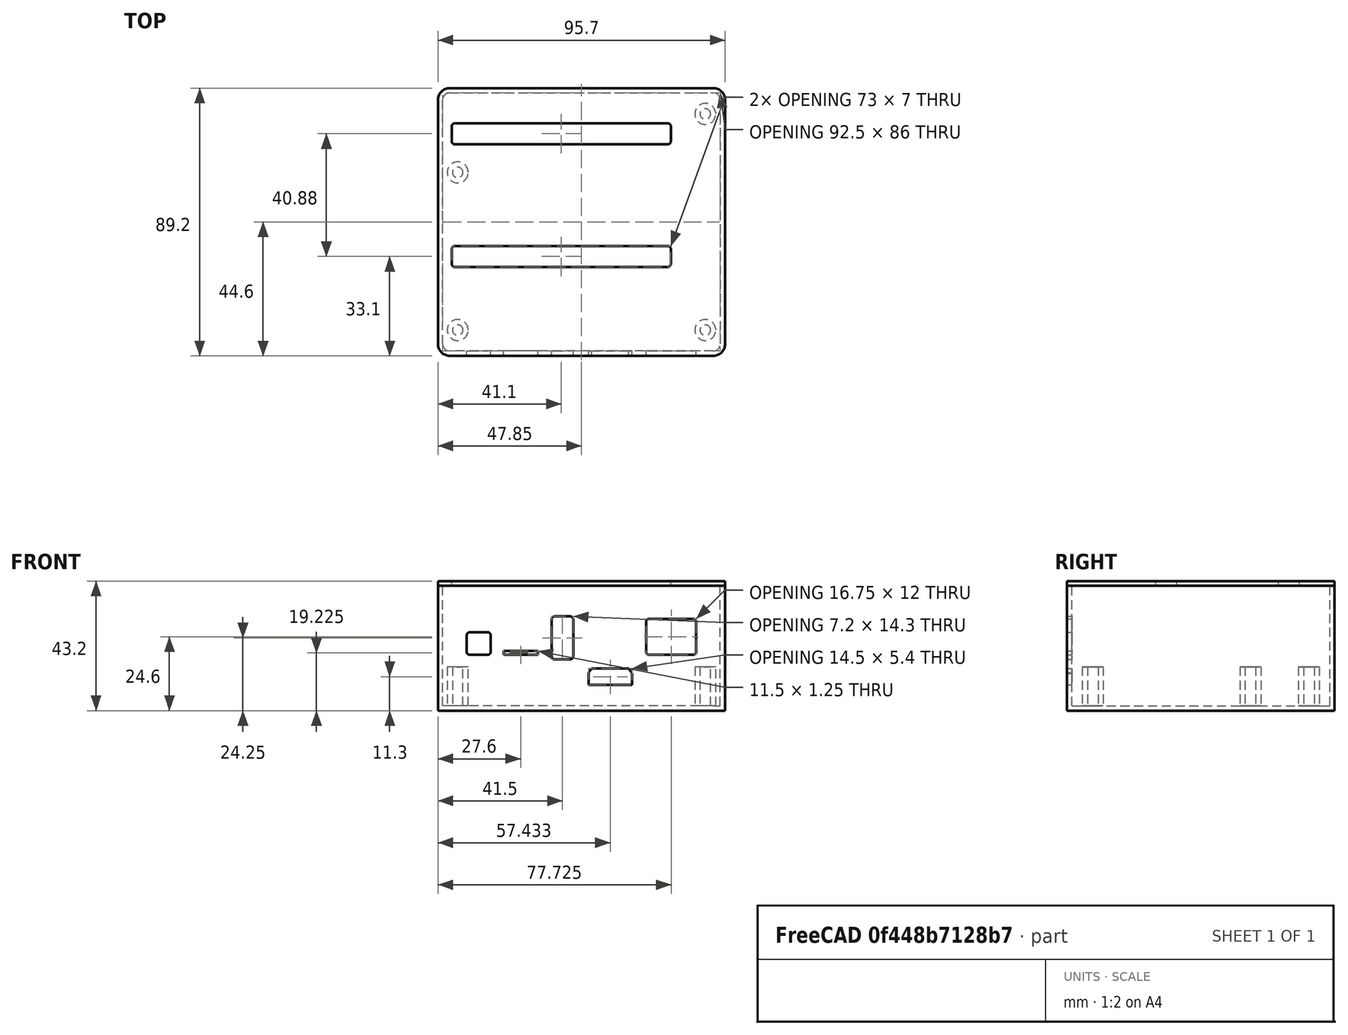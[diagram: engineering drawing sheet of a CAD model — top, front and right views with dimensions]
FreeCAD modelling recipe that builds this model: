
FCSTD DOCUMENT  (FreeCAD 0.16R6712 (Git))
Label: odroid-hc4-enclosure-with-lid
License: All rights reserved
LicenseURL: http://en.wikipedia.org/wiki/All_rights_reserved
objects: Sketcher::SketchObject×6, PartDesign::Pad×5, Part::Thickness×1, Part::Cut×1, PartDesign::Fillet×1, Mesh::Feature×1, Part::Part2DObjectPython×1
note: 20 computed .brp shape members not serialized (recipe doc carries the construction recipe); baked Part::Feature solids carry a one-line shape summary decoded from their .brp

FEATURE [Sketcher::SketchObject] Sketch  label="Sketch - Board"
  expr: Constraints[50] = Sketch.Constraints.SataX
  expr: Constraints[51] = Sketch.Constraints.SataY
  expr: Constraints[52] = Sketch.Constraints.SataOffsetX
  sketch-geometry (20):
    g0: LineSegment StartX=-39.25 StartY=42 StartZ=0 EndX=39.25 EndY=42 EndZ=0
    g1: LineSegment StartX=45.25 StartY=36 StartZ=0 EndX=45.25 EndY=-36 EndZ=0
    g2: LineSegment StartX=39.25 StartY=-42 StartZ=0 EndX=-39.25 EndY=-42 EndZ=0
    g3: LineSegment StartX=-45.25 StartY=-36 StartZ=0 EndX=-45.25 EndY=36 EndZ=0
    g4: ArcOfCircle CenterX=-39.25 CenterY=-36 CenterZ=0 NormalX=0 NormalY=0 NormalZ=1 Radius=6 StartAngle=3.14159 EndAngle=4.71239
    g5: ArcOfCircle CenterX=39.25 CenterY=-36 CenterZ=0 NormalX=0 NormalY=0 NormalZ=1 Radius=6 StartAngle=4.71239 EndAngle=6.28319
    g6: ArcOfCircle CenterX=39.25 CenterY=36 CenterZ=0 NormalX=0 NormalY=0 NormalZ=1 Radius=6 StartAngle=0 EndAngle=1.5708
    g7: ArcOfCircle CenterX=-39.25 CenterY=36 CenterZ=0 NormalX=0 NormalY=0 NormalZ=1 Radius=6 StartAngle=1.5708 EndAngle=3.14159
    g8: Circle CenterX=-41.25 CenterY=-36 CenterZ=0 NormalX=0 NormalY=0 NormalZ=1 Radius=1.75
    g9: Circle CenterX=41.25 CenterY=-36 CenterZ=0 NormalX=0 NormalY=0 NormalZ=1 Radius=1.75
    g10: Circle CenterX=-41.25 CenterY=16.5 CenterZ=0 NormalX=0 NormalY=0 NormalZ=1 Radius=1.75
    g11: Circle CenterX=41.25 CenterY=36 CenterZ=0 NormalX=0 NormalY=0 NormalZ=1 Radius=1.75
    g12: LineSegment StartX=-24.4 StartY=-9 StartZ=0 EndX=19.25 EndY=-9 EndZ=0
    g13: LineSegment StartX=19.25 StartY=-9 StartZ=0 EndX=19.25 EndY=-14 EndZ=0
    g14: LineSegment StartX=19.25 StartY=-14 StartZ=0 EndX=-24.4 EndY=-14 EndZ=0
    g15: LineSegment StartX=-24.4 StartY=-14 StartZ=0 EndX=-24.4 EndY=-9 EndZ=0
    g16: LineSegment StartX=-24.4 StartY=31.88 StartZ=0 EndX=19.25 EndY=31.88 EndZ=0
    g17: LineSegment StartX=19.25 StartY=31.88 StartZ=0 EndX=19.25 EndY=26.88 EndZ=0
    g18: LineSegment StartX=19.25 StartY=26.88 StartZ=0 EndX=-24.4 EndY=26.88 EndZ=0
    g19: LineSegment StartX=-24.4 StartY=26.88 StartZ=0 EndX=-24.4 EndY=31.88 EndZ=0
  constraints (54):
    c: Horizontal(g0)
    c: Horizontal(g2)
    c: Vertical(g1)
    c: Vertical(g3)
    c: Tangent(g3,g4) = 1.5708
    c: Tangent(g2,g4) = 1.5708
    c: Tangent(g2,g5) = 1.5708
    c: Tangent(g1,g5) = 1.5708
    c: Tangent(g0,g6) = 1.5708
    c: Tangent(g1,g6) = 1.5708
    c: Tangent(g3,g7) = 1.5708
    c: Tangent(g0,g7) = 1.5708
    c: Symmetric(g3,g1,g-2)
    c: Symmetric(g2,g0,g-1)
    c: Radius(g6) = 6
    c: Equal(g6,g7)
    c: DistanceX(g3,g1) = 90.5  'X'
    c: DistanceY(g2,g0) = 84  'Y'
    c: Radius(g9) = 1.75  'Constraint20'
    c: Equal(g9,g8)
    c: Equal(g9,g10)
    c: Equal(g9,g11)
    c: DistanceY(g2,g9) = 6  'Y1'
    c: DistanceX(g9,g1) = 4  'X1'
    c: DistanceY(g2,g8) = 6  'Y4'
    c: DistanceX(g3,g8) = 4  'X4'
    c: DistanceX(g11,g1) = 4  'X2'
    c: DistanceY(g11,g0) = 6  'Y2'
    c: DistanceX(g3,g10) = 4  'X3'
    c: DistanceY(g10,g0) = 25.5  'Y3'
    c: Coincident(g12,g13)
    c: Coincident(g13,g14)
    c: Coincident(g14,g15)
    c: Coincident(g15,g12)
    c: Horizontal(g12)
    c: Horizontal(g14)
    c: Vertical(g13)
    c: Vertical(g15)
    c: DistanceX(g14,g13) = 43.65  'SataX'
    c: DistanceX(g13,g1) = 26  'SataOffsetX'
    c: DistanceY(g14,g12) = 5  'SataY'
    c: DistanceY(g2,g13) = 28  'SataoffsetY'
    c: Coincident(g16,g17)
    c: Coincident(g17,g18)
    c: Coincident(g18,g19)
    c: Coincident(g19,g16)
    c: Horizontal(g16)
    c: Horizontal(g18)
    c: Vertical(g17)
    c: Vertical(g19)
    c: DistanceX(g18,g17) = 43.65
    c: DistanceY(g18,g16) = 5
    c: DistanceX(g17,g1) = 26
    c: DistanceY(g16,g0) = 10.12  'Sata2OffsetY'
FEATURE [Sketcher::SketchObject] Sketch001  label="Sketch - Walls"
  expr: Constraints.X = Sketch.Constraints.X + 2 + 3.2
  expr: Constraints.Y = Sketch.Constraints.Y + 2 + 3.2
  sketch-geometry (8):
    g0: LineSegment StartX=-43.85 StartY=44.6 StartZ=0 EndX=43.85 EndY=44.6 EndZ=0
    g1: LineSegment StartX=47.85 StartY=40.6 StartZ=0 EndX=47.85 EndY=-40.6 EndZ=0
    g2: LineSegment StartX=43.85 StartY=-44.6 StartZ=0 EndX=-43.85 EndY=-44.6 EndZ=0
    g3: LineSegment StartX=-47.85 StartY=-40.6 StartZ=0 EndX=-47.85 EndY=40.6 EndZ=0
    g4: ArcOfCircle CenterX=-43.85 CenterY=-40.6 CenterZ=0 NormalX=0 NormalY=0 NormalZ=1 Radius=4 StartAngle=3.14159 EndAngle=4.71239
    g5: ArcOfCircle CenterX=43.85 CenterY=-40.6 CenterZ=0 NormalX=0 NormalY=0 NormalZ=1 Radius=4 StartAngle=4.71239 EndAngle=6.28319
    g6: ArcOfCircle CenterX=43.85 CenterY=40.6 CenterZ=0 NormalX=0 NormalY=0 NormalZ=1 Radius=4 StartAngle=0 EndAngle=1.5708
    g7: ArcOfCircle CenterX=-43.85 CenterY=40.6 CenterZ=0 NormalX=0 NormalY=0 NormalZ=1 Radius=4 StartAngle=1.5708 EndAngle=3.14159
  constraints (19):
    c: Horizontal(g0)
    c: Horizontal(g2)
    c: Vertical(g1)
    c: Vertical(g3)
    c: Tangent(g3,g4) = 1.5708
    c: Tangent(g2,g4) = 1.5708
    c: Tangent(g2,g5) = 1.5708
    c: Tangent(g1,g5) = 1.5708
    c: Tangent(g1,g6) = 1.5708
    c: Tangent(g0,g6) = 1.5708
    c: Tangent(g3,g7) = 1.5708
    c: Tangent(g0,g7) = 1.5708
    c: Radius(g7) = 4
    c: Equal(g7,g6)
    c: Equal(g7,g5)
    c: DistanceX(g3,g1) = 95.7  'X'
    c: DistanceY(g2,g0) = 89.2  'Y'
    c: Symmetric(g2,g0,g-1)  'Constraint18'
    c: Symmetric(g3,g1,g-2)
FEATURE [PartDesign::Pad] Pad
  Length = 40
  Length2 = 1.6
  Sketch = -> Sketch001
  Type = 4
FEATURE [Part::Thickness] Thickness
  Faces = -> Pad [Face10]
  Intersection = false
  Join = 0
  Mode = 0
  SelfIntersection = false
  Value = -1.6
FEATURE [Sketcher::SketchObject] Sketch002  label="Sketch - Legs"
  Support = -> Thickness [Face19]
  expr: Constraints[24] = Sketch.Constraints.Y4
  expr: Constraints[29] = Sketch.Constraints.Y3
  expr: Constraints[28] = Sketch.Constraints.X3
  expr: Constraints[26] = Sketch.Constraints.X2
  expr: Constraints[27] = Sketch.Constraints.Y2
  expr: Constraints[25] = Sketch.Constraints.X4
  expr: Constraints[22] = Sketch.Constraints.Y1
  expr: Constraints.Y = Sketch.Constraints.Y
  expr: Constraints[23] = Sketch.Constraints.X1
  expr: Constraints.X = Sketch.Constraints.X
  sketch-geometry (12):
    g0: LineSegment [constr] StartX=-39.25 StartY=42 StartZ=0 EndX=39.25 EndY=42 EndZ=0
    g1: LineSegment [constr] StartX=45.25 StartY=36 StartZ=0 EndX=45.25 EndY=-36 EndZ=0
    g2: LineSegment [constr] StartX=39.25 StartY=-42 StartZ=0 EndX=-39.25 EndY=-42 EndZ=0
    g3: LineSegment [constr] StartX=-45.25 StartY=-36 StartZ=0 EndX=-45.25 EndY=36 EndZ=0
    g4: ArcOfCircle [constr] CenterX=-39.25 CenterY=-36 CenterZ=0 NormalX=0 NormalY=0 NormalZ=1 Radius=6 StartAngle=3.14159 EndAngle=4.71239
    g5: ArcOfCircle [constr] CenterX=39.25 CenterY=-36 CenterZ=0 NormalX=0 NormalY=0 NormalZ=1 Radius=6 StartAngle=4.71239 EndAngle=6.28319
    g6: ArcOfCircle [constr] CenterX=39.25 CenterY=36 CenterZ=0 NormalX=0 NormalY=0 NormalZ=1 Radius=6 StartAngle=0 EndAngle=1.5708
    g7: ArcOfCircle [constr] CenterX=-39.25 CenterY=36 CenterZ=0 NormalX=0 NormalY=0 NormalZ=1 Radius=6 StartAngle=1.5708 EndAngle=3.14159
    g8: Circle CenterX=-41.25 CenterY=-36 CenterZ=0 NormalX=0 NormalY=0 NormalZ=1 Radius=1.75
    g9: Circle CenterX=41.25 CenterY=-36 CenterZ=0 NormalX=0 NormalY=0 NormalZ=1 Radius=1.75
    g10: Circle CenterX=-41.25 CenterY=16.5 CenterZ=0 NormalX=0 NormalY=0 NormalZ=1 Radius=1.75
    g11: Circle CenterX=41.25 CenterY=36 CenterZ=0 NormalX=0 NormalY=0 NormalZ=1 Radius=1.75
  constraints (30):
    c: Horizontal(g0)
    c: Horizontal(g2)
    c: Vertical(g1)
    c: Vertical(g3)
    c: Tangent(g3,g4) = 1.5708
    c: Tangent(g2,g4) = 1.5708
    c: Tangent(g2,g5) = 1.5708
    c: Tangent(g1,g5) = 1.5708
    c: Tangent(g0,g6) = 1.5708
    c: Tangent(g1,g6) = 1.5708
    c: Tangent(g3,g7) = 1.5708
    c: Tangent(g0,g7) = 1.5708
    c: Symmetric(g3,g1,g-2)
    c: Symmetric(g2,g0,g-1)
    c: Radius(g6) = 6
    c: Equal(g6,g7)
    c: DistanceX(g3,g1) = 90.5  'X'
    c: DistanceY(g2,g0) = 84  'Y'
    c: Radius(g9) = 1.75  'Constraint20'
    c: Equal(g9,g8)
    c: Equal(g9,g10)
    c: Equal(g9,g11)
    c: DistanceY(g2,g9) = 6
    c: DistanceX(g9,g1) = 4
    c: DistanceY(g2,g8) = 6
    c: DistanceX(g3,g8) = 4
    c: DistanceX(g11,g1) = 4
    c: DistanceY(g11,g0) = 6
    c: DistanceX(g3,g10) = 4
    c: DistanceY(g10,g0) = 25.5
FEATURE [PartDesign::Pad] Pad001
  Length = 13
  Length2 = 100
  Sketch = -> Sketch002
  Type = 0
FEATURE [Sketcher::SketchObject] Sketch003  label="Sketch - Wide Legs"
  ExternalGeometry = -> [Pad001]
  Support = -> Pad001 [Face19]
  sketch-geometry (4):
    g0: Circle CenterX=41.25 CenterY=-36 CenterZ=0 NormalX=0 NormalY=0 NormalZ=1 Radius=3.5
    g1: Circle CenterX=41.25 CenterY=36 CenterZ=0 NormalX=0 NormalY=0 NormalZ=1 Radius=3.5
    g2: Circle CenterX=-41.25 CenterY=16.5 CenterZ=0 NormalX=0 NormalY=0 NormalZ=1 Radius=3.5
    g3: Circle CenterX=-41.25 CenterY=-36 CenterZ=0 NormalX=0 NormalY=0 NormalZ=1 Radius=3.5
  constraints (8):
    c: Coincident(g0,g-5)
    c: Coincident(g1,g-6)
    c: Coincident(g2,g-3)
    c: Coincident(g3,g-4)
    c: Radius(g2) = 3.5
    c: Equal(g2,g1)
    c: Equal(g2,g0)
    c: Equal(g2,g3)
FEATURE [PartDesign::Pad] Pad002
  Length = 13
  Length2 = 100
  Sketch = -> Sketch003
  Type = 0
FEATURE [Sketcher::SketchObject] Sketch004
  Placement = pos=(0,-44.6,0) rot=(1,0,0;1.5708rad)
  sketch-geometry (40):
    g0: LineSegment StartX=22.5 StartY=29 StartZ=0 EndX=37.25 EndY=29 EndZ=0
    g1: LineSegment StartX=38.25 StartY=28 StartZ=0 EndX=38.25 EndY=18 EndZ=0
    g2: LineSegment StartX=37.25 StartY=17 StartZ=0 EndX=22.5 EndY=17 EndZ=0
    g3: LineSegment StartX=21.5 StartY=18 StartZ=0 EndX=21.5 EndY=28 EndZ=0
    g4: LineSegment StartX=-8.95 StartY=29.8 StartZ=0 EndX=-3.75 EndY=29.8 EndZ=0
    g5: LineSegment StartX=-2.75 StartY=28.8 StartZ=0 EndX=-2.75 EndY=16.5 EndZ=0
    g6: LineSegment StartX=-3.75 StartY=15.5 StartZ=0 EndX=-8.95 EndY=15.5 EndZ=0
    g7: LineSegment StartX=-9.95 StartY=16.5 StartZ=0 EndX=-9.95 EndY=28.8 EndZ=0
    g8: LineSegment StartX=-37.25 StartY=24.5 StartZ=0 EndX=-31.25 EndY=24.5 EndZ=0
    g9: LineSegment StartX=-30.25 StartY=23.5 StartZ=0 EndX=-30.25 EndY=18 EndZ=0
    g10: LineSegment StartX=-31.25 StartY=17 StartZ=0 EndX=-37.25 EndY=17 EndZ=0
    g11: LineSegment StartX=-38.25 StartY=18 StartZ=0 EndX=-38.25 EndY=23.5 EndZ=0
    g12: LineSegment StartX=-26 StartY=18.25 StartZ=0 EndX=-14.5 EndY=18.25 EndZ=0
    g13: LineSegment StartX=-14.5 StartY=18.25 StartZ=0 EndX=-14.5 EndY=17 EndZ=0
    g14: LineSegment StartX=-14.5 StartY=17 StartZ=0 EndX=-26 EndY=17 EndZ=0
    g15: LineSegment StartX=-26 StartY=17 StartZ=0 EndX=-26 EndY=18.25 EndZ=0
    g16: ArcOfCircle CenterX=37.25 CenterY=18 CenterZ=0 NormalX=0 NormalY=0 NormalZ=1 Radius=1 StartAngle=4.71239 EndAngle=6.28319
    g17: ArcOfCircle CenterX=37.25 CenterY=28 CenterZ=0 NormalX=0 NormalY=0 NormalZ=1 Radius=1 StartAngle=0 EndAngle=1.5708
    g18: ArcOfCircle CenterX=22.5 CenterY=28 CenterZ=0 NormalX=0 NormalY=0 NormalZ=1 Radius=1 StartAngle=1.5708 EndAngle=3.14159
    g19: ArcOfCircle CenterX=22.5 CenterY=18 CenterZ=0 NormalX=0 NormalY=0 NormalZ=1 Radius=1 StartAngle=3.14159 EndAngle=4.71239
    g20: ArcOfCircle CenterX=-8.95 CenterY=16.5 CenterZ=0 NormalX=0 NormalY=0 NormalZ=1 Radius=1 StartAngle=3.14159 EndAngle=4.71239
    g21: ArcOfCircle CenterX=-3.75 CenterY=16.5 CenterZ=0 NormalX=0 NormalY=0 NormalZ=1 Radius=1 StartAngle=4.71239 EndAngle=6.28319
    g22: ArcOfCircle CenterX=-3.75 CenterY=28.8 CenterZ=0 NormalX=0 NormalY=0 NormalZ=1 Radius=1 StartAngle=0 EndAngle=1.5708
    g23: ArcOfCircle CenterX=-8.95 CenterY=28.8 CenterZ=0 NormalX=0 NormalY=0 NormalZ=1 Radius=1 StartAngle=1.5708 EndAngle=3.14159
    g24: ArcOfCircle CenterX=-37.25 CenterY=18 CenterZ=0 NormalX=0 NormalY=0 NormalZ=1 Radius=1 StartAngle=3.14159 EndAngle=4.71239
    g25: ArcOfCircle CenterX=-31.25 CenterY=18 CenterZ=0 NormalX=0 NormalY=0 NormalZ=1 Radius=1 StartAngle=4.71239 EndAngle=6.28319
    g26: ArcOfCircle CenterX=-31.25 CenterY=23.5 CenterZ=0 NormalX=0 NormalY=0 NormalZ=1 Radius=1 StartAngle=0 EndAngle=1.5708
    g27: ArcOfCircle CenterX=-37.25 CenterY=23.5 CenterZ=0 NormalX=0 NormalY=0 NormalZ=1 Radius=1 StartAngle=1.5708 EndAngle=3.14159
    g28: GeomPoint [constr] X=2.3334 Y=7 Z=0
    g29: GeomPoint [constr] X=16.8334 Y=7 Z=0
    g30: GeomPoint [constr] X=2.3334 Y=11.0069 Z=0
    g31: GeomPoint [constr] X=3.39176 Y=12.4 Z=0
    g32: GeomPoint [constr] X=15.7519 Y=12.4 Z=0
    g33: GeomPoint [constr] X=16.8334 Y=10.8557 Z=0
    g34: LineSegment StartX=2.3334 StartY=7 StartZ=0 EndX=2.3334 EndY=11.0069 EndZ=0
    g35: LineSegment StartX=2.3334 StartY=11.0069 StartZ=0 EndX=3.39176 EndY=12.4 EndZ=0
    g36: LineSegment StartX=3.39176 StartY=12.4 StartZ=0 EndX=15.7519 EndY=12.4 EndZ=0
    g37: LineSegment StartX=15.7519 StartY=12.4 StartZ=0 EndX=16.8334 EndY=10.8557 EndZ=0
    g38: LineSegment StartX=16.8334 StartY=10.8557 StartZ=0 EndX=16.8334 EndY=7 EndZ=0
    g39: LineSegment StartX=16.8334 StartY=7 StartZ=0 EndX=2.3334 EndY=7 EndZ=0
  constraints (91):
    c: Horizontal(g0)
    c: Horizontal(g2)
    c: Vertical(g1)
    c: Vertical(g3)
    c: Horizontal(g4)
    c: Horizontal(g6)
    c: Vertical(g5)
    c: Vertical(g7)
    c: Horizontal(g8)
    c: Horizontal(g10)
    c: Vertical(g9)
    c: Vertical(g11)
    c: Coincident(g12,g13)
    c: Coincident(g13,g14)
    c: Coincident(g14,g15)
    c: Coincident(g15,g12)
    c: Horizontal(g12)
    c: Horizontal(g14)
    c: Vertical(g13)
    c: Vertical(g15)
    c: DistanceX(g14,g-1) = 26
    c: DistanceX(g14,g14) = 11.5
    c: Tangent(g2,g16) = 1.5708
    c: Tangent(g1,g16) = 1.5708
    c: Tangent(g0,g17) = 1.5708
    c: Tangent(g1,g17) = 1.5708
    c: Tangent(g3,g18) = 1.5708
    c: Tangent(g0,g18) = 1.5708
    c: Tangent(g3,g19) = 1.5708
    c: Tangent(g2,g19) = 1.5708
    c: DistanceX(g-1,g1) = 38.25
    c: DistanceX(g3,g1) = 16.75
    c: DistanceY(g2,g0) = 12
    c: DistanceY(g-1,g2) = 17
    c: Radius(g17) = 1
    c: Equal(g17,g16)
    c: Equal(g17,g19)
    c: Equal(g17,g18)
    c: Tangent(g7,g20) = 1.5708
    c: Tangent(g6,g20) = 1.5708
    c: Tangent(g6,g21) = 1.5708
    c: Tangent(g5,g21) = 1.5708
    c: Tangent(g4,g22) = 1.5708
    c: Tangent(g5,g22) = 1.5708
    c: Tangent(g7,g23) = 1.5708
    c: Tangent(g4,g23) = 1.5708
    c: DistanceX(g5,g-1) = 2.75
    c: DistanceY(g-1,g6) = 15.5
    c: DistanceX(g7,g5) = 7.2
    c: DistanceY(g6,g4) = 14.3
    c: Radius(g21) = 1
    c: Equal(g21,g22)
    c: Equal(g21,g23)
    c: Equal(g21,g20)
    c: Tangent(g11,g24) = 1.5708
    c: Tangent(g10,g24) = 1.5708
    c: Tangent(g10,g25) = 1.5708
    c: Tangent(g9,g25) = 1.5708
    c: Tangent(g9,g26) = 1.5708
    c: Tangent(g8,g26) = 1.5708
    c: Tangent(g11,g27) = 1.5708
    c: Tangent(g8,g27) = 1.5708
    c: DistanceX(g9,g-1) = 30.25
    c: DistanceY(g10,g8) = 7.5
    c: DistanceX(g11,g9) = 8
    c: DistanceY(g-1,g10) = 17
    c: Radius(g25) = 1
    c: Equal(g25,g24)
    c: Equal(g25,g27)
    c: Equal(g25,g26)
    c: DistanceY(g-1,g14) = 17
    c: DistanceY(g14,g12) = 1.25
    c: Coincident(g34,g28)
    c: Coincident(g34,g30)
    c: Vertical(g34)
    c: Coincident(g34,g35)
    c: Coincident(g35,g31)
    c: Coincident(g35,g36)
    c: Coincident(g36,g32)
    c: Horizontal(g36)
    c: Coincident(g36,g37)
    c: Coincident(g37,g33)
    c: Coincident(g37,g38)
    c: Coincident(g38,g29)
    c: Vertical(g38)
    c: Coincident(g38,g39)
    c: Coincident(g39,g34)
    c: Horizontal(g39)
    c: DistanceX(g28,g29) = 14.5
    c: DistanceY(g-1,g28) = 7
    c: DistanceY(g28,g31) = 5.4
FEATURE [PartDesign::Pad] Pad003
  Length = 3
  Length2 = 100
  Placement = pos=(0,-44.6,0) rot=(1,0,0;1.5708rad)
  Reversed = true
  Sketch = -> Sketch004
  Type = 0
FEATURE [Part::Cut] Cut
  Base = -> Pad002
  Tool = -> Pad003
FEATURE [PartDesign::Fillet] Fillet
  Base = -> Cut [Edge3,Edge9,Edge11,Edge12,Edge13,Edge14,Edge15,Edge6]
  Radius = 0.6
FEATURE [Mesh::Feature] Odroid_HC4  label="Odroid-HC4"
  Placement = pos=(-45.25,-42,11) rot=(0,0,1;0rad)
FEATURE [Sketcher::SketchObject] Sketch005  label="Sketch - Top Lid"
  Placement = pos=(0,0,40) rot=(0,0,1;0rad)
  Support = -> Pad [Face10]
  expr: Constraints[58] = Sketch.Constraints.Sata2OffsetY + 1 + 1.6 - 1
  expr: Constraints.Y = Sketch.Constraints.Y + 2 + 3.2
  expr: Constraints.X = Sketch.Constraints.X + 2 + 3.2
  sketch-geometry (24):
    g0: LineSegment StartX=-43.85 StartY=44.6 StartZ=0 EndX=43.85 EndY=44.6 EndZ=0
    g1: LineSegment StartX=47.85 StartY=40.6 StartZ=0 EndX=47.85 EndY=-40.6 EndZ=0
    g2: LineSegment StartX=43.85 StartY=-44.6 StartZ=0 EndX=-43.85 EndY=-44.6 EndZ=0
    g3: LineSegment StartX=-47.85 StartY=-40.6 StartZ=0 EndX=-47.85 EndY=40.6 EndZ=0
    g4: ArcOfCircle CenterX=-43.85 CenterY=-40.6 CenterZ=0 NormalX=0 NormalY=0 NormalZ=1 Radius=4 StartAngle=3.14159 EndAngle=4.71239
    g5: ArcOfCircle CenterX=43.85 CenterY=-40.6 CenterZ=0 NormalX=0 NormalY=0 NormalZ=1 Radius=4 StartAngle=4.71239 EndAngle=6.28319
    g6: ArcOfCircle CenterX=43.85 CenterY=40.6 CenterZ=0 NormalX=0 NormalY=0 NormalZ=1 Radius=4 StartAngle=0 EndAngle=1.5708
    g7: ArcOfCircle CenterX=-43.85 CenterY=40.6 CenterZ=0 NormalX=0 NormalY=0 NormalZ=1 Radius=4 StartAngle=1.5708 EndAngle=3.14159
    g8: LineSegment StartX=-42.25 StartY=-8 StartZ=0 EndX=28.75 EndY=-8 EndZ=0
    g9: LineSegment StartX=29.75 StartY=-9 StartZ=0 EndX=29.75 EndY=-14 EndZ=0
    g10: LineSegment StartX=28.75 StartY=-15 StartZ=0 EndX=-42.25 EndY=-15 EndZ=0
    g11: LineSegment StartX=-43.25 StartY=-14 StartZ=0 EndX=-43.25 EndY=-9 EndZ=0
    g12: ArcOfCircle CenterX=-42.25 CenterY=-9 CenterZ=0 NormalX=0 NormalY=0 NormalZ=1 Radius=1 StartAngle=1.5708 EndAngle=3.14159
    g13: ArcOfCircle CenterX=-42.25 CenterY=-14 CenterZ=0 NormalX=0 NormalY=0 NormalZ=1 Radius=1 StartAngle=3.14159 EndAngle=4.71239
    g14: ArcOfCircle CenterX=28.75 CenterY=-14 CenterZ=0 NormalX=0 NormalY=0 NormalZ=1 Radius=1 StartAngle=4.71239 EndAngle=6.28319
    g15: ArcOfCircle CenterX=28.75 CenterY=-9 CenterZ=0 NormalX=0 NormalY=0 NormalZ=1 Radius=1 StartAngle=0 EndAngle=1.5708
    g16: LineSegment StartX=-42.25 StartY=32.88 StartZ=0 EndX=28.75 EndY=32.88 EndZ=0
    g17: LineSegment StartX=29.75 StartY=31.88 StartZ=0 EndX=29.75 EndY=26.88 EndZ=0
    g18: LineSegment StartX=28.75 StartY=25.88 StartZ=0 EndX=-42.25 EndY=25.88 EndZ=0
    g19: LineSegment StartX=-43.25 StartY=26.88 StartZ=0 EndX=-43.25 EndY=31.88 EndZ=0
    g20: ArcOfCircle CenterX=28.75 CenterY=26.88 CenterZ=0 NormalX=0 NormalY=0 NormalZ=1 Radius=1 StartAngle=4.71239 EndAngle=6.28319
    g21: ArcOfCircle CenterX=28.75 CenterY=31.88 CenterZ=0 NormalX=0 NormalY=0 NormalZ=1 Radius=1 StartAngle=0 EndAngle=1.5708
    g22: ArcOfCircle CenterX=-42.25 CenterY=31.88 CenterZ=0 NormalX=0 NormalY=0 NormalZ=1 Radius=1 StartAngle=1.5708 EndAngle=3.14159
    g23: ArcOfCircle CenterX=-42.25 CenterY=26.88 CenterZ=0 NormalX=0 NormalY=0 NormalZ=1 Radius=1 StartAngle=3.14159 EndAngle=4.71239
  constraints (59):
    c: Horizontal(g0)
    c: Horizontal(g2)
    c: Vertical(g1)
    c: Vertical(g3)
    c: Tangent(g3,g4) = 1.5708
    c: Tangent(g2,g4) = 1.5708
    c: Tangent(g2,g5) = 1.5708
    c: Tangent(g1,g5) = 1.5708
    c: Tangent(g1,g6) = 1.5708
    c: Tangent(g0,g6) = 1.5708
    c: Tangent(g3,g7) = 1.5708
    c: Tangent(g0,g7) = 1.5708
    c: Radius(g7) = 4
    c: Equal(g7,g6)
    c: Equal(g7,g5)
    c: DistanceX(g3,g1) = 95.7  'X'
    c: DistanceY(g2,g0) = 89.2  'Y'
    c: Symmetric(g2,g0,g-1)  'Constraint18'
    c: Symmetric(g3,g1,g-2)
    c: Horizontal(g8)
    c: Horizontal(g10)
    c: Vertical(g9)
    c: Vertical(g11)
    c: Tangent(g11,g12) = 1.5708  'Constraint29'
    c: Tangent(g8,g12) = 1.5708  'Constraint25'
    c: Tangent(g11,g13) = 1.5708  'Constraint27'
    c: Tangent(g10,g13) = 1.5708
    c: Tangent(g10,g14) = 1.5708
    c: Tangent(g9,g14) = 1.5708
    c: Tangent(g8,g15) = 1.5708
    c: Tangent(g9,g15) = 1.5708
    c: DistanceY(g2,g10) = 29.6
    c: DistanceX(g9,g1) = 18.1
    c: DistanceY(g10,g8) = 7
    c: DistanceX(g11,g9) = 73
    c: Radius(g13) = 1
    c: Equal(g13,g12)
    c: Equal(g13,g15)
    c: Equal(g13,g14)
    c: Horizontal(g16)
    c: Horizontal(g18)
    c: Vertical(g17)
    c: Vertical(g19)
    c: Tangent(g18,g20) = 1.5708
    c: Tangent(g17,g20) = 1.5708
    c: Tangent(g16,g21) = 1.5708
    c: Tangent(g17,g21) = 1.5708
    c: Tangent(g19,g22) = 1.5708
    c: Tangent(g16,g22) = 1.5708
    c: Tangent(g19,g23) = 1.5708
    c: Tangent(g18,g23) = 1.5708
    c: Radius(g22) = 1
    c: Equal(g22,g23)
    c: Equal(g22,g20)
    c: Equal(g22,g21)
    c: DistanceY(g18,g16) = 7
    c: DistanceX(g19,g17) = 73
    c: DistanceX(g17,g1) = 18.1
    c: DistanceY(g16,g0) = 11.72
FEATURE [Part::Part2DObjectPython] Clone2D  label="Clone of Sketch - Top Lid (2D)"  # Draft 2D object (typed FeaturePython)
  Objects = -> [Sketch005]
  Placement = pos=(0,0,40) rot=(0,0,1;0rad)
  Scale = (1,1,1)
FEATURE [PartDesign::Pad] Pad004
  Length = 1.6
  Length2 = 100
  Placement = pos=(0,0,40) rot=(0,0,1;0rad)
  Sketch = -> Clone2D
  Type = 0
